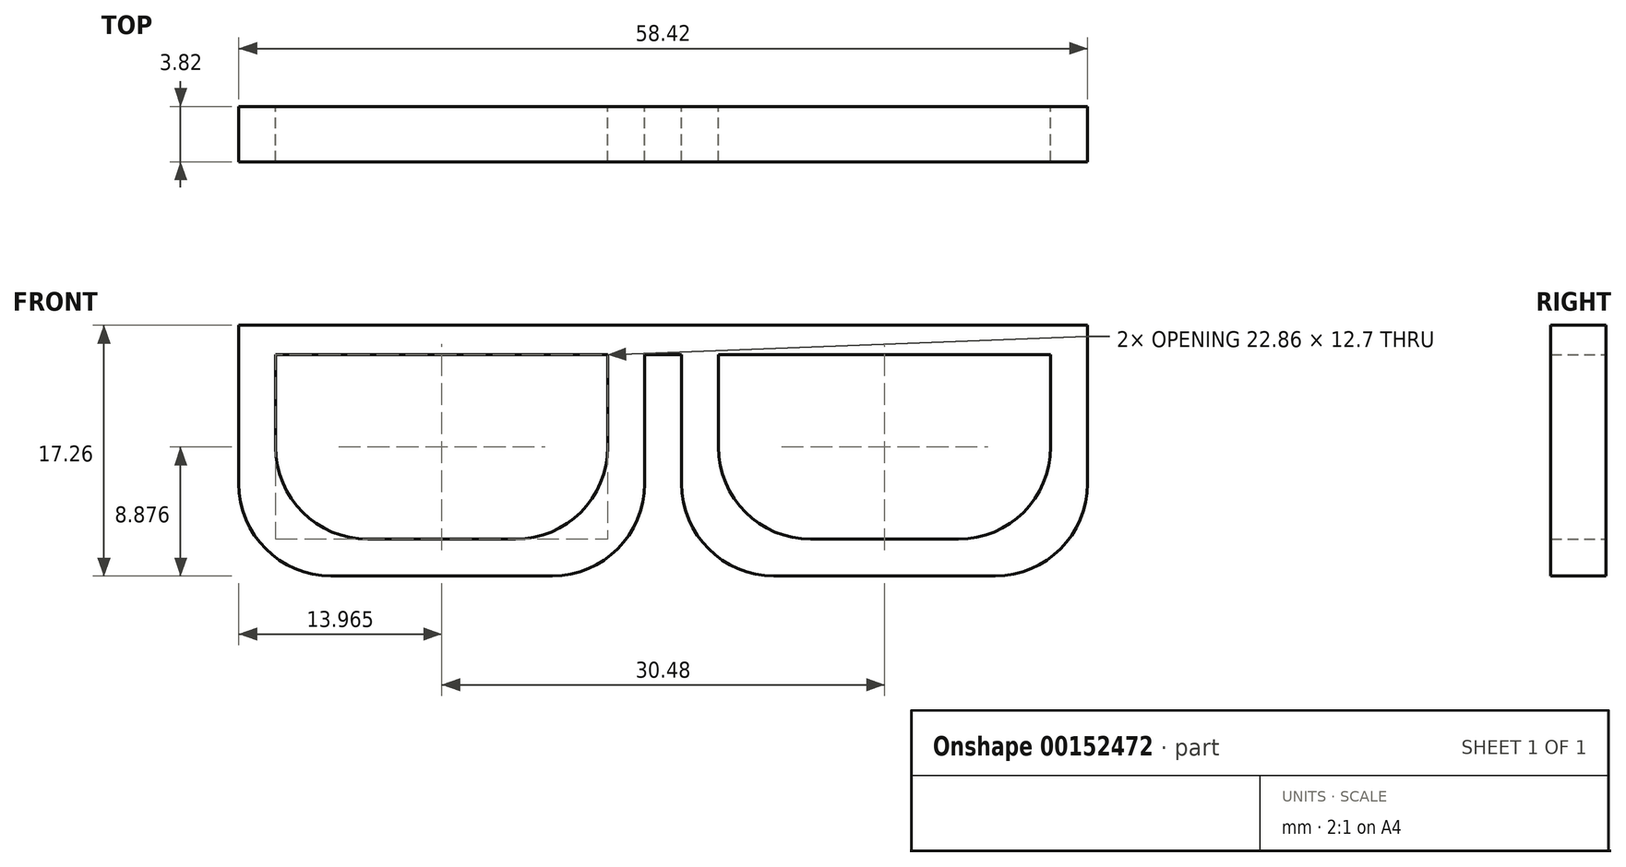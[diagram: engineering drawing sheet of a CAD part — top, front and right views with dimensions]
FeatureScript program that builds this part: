
annotation { "Feature Type Name" : "Feature", "Feature Type Description" : "" }
export const myFeature = defineFeature(function(context is Context, id is Id, definition is map)
    precondition{}
    {
        {
            var Q0;
            Q0=qCreatedBy(makeId("Front.planeOp"),FACE);
            var sketch = newSketch(context, id + "F0", { "sketchPlane" : qUnion([Q0])});
            skLineSegment(sketch, "E0", {"start": v(-55.8, 24.47) * mm, "end": v(-32.94, 24.47) * mm});
            skLineSegment(sketch, "E1", {"start": v(-32.94, 24.47) * mm, "end": v(-32.94, 18.12) * mm});
            skLineSegment(sketch, "E2", {"start": v(-39.3, 11.77) * mm, "end": v(-49.45, 11.77) * mm});
            skLineSegment(sketch, "E3", {"start": v(-55.8, 18.12) * mm, "end": v(-55.8, 24.47) * mm});
            skLineSegment(sketch, "E4", {"start": v(-55.8, 24.47) * mm, "end": v(-2.46, 24.47) * mm});
            skLineSegment(sketch, "E5", {"start": v(-2.46, 24.47) * mm, "end": v(-2.46, 18.12) * mm});
            skLineSegment(sketch, "E6", {"start": v(-8.81, 11.77) * mm, "end": v(-18.97, 11.77) * mm});
            skLineSegment(sketch, "E7", {"start": v(-25.32, 18.12) * mm, "end": v(-25.32, 24.47) * mm});
            skLineSegment(sketch, "E8", {"start": v(-32.94, 22.23) * mm, "end": v(-25.32, 22.23) * mm});
            skPoint(sketch, "E9.visualSharp", {"position": v(-2.46, 11.77) * mm});
            skArc(sketch, "E9.filletArc", {"start": v(-8.81, 11.77) * mm, "mid": v(-4.32, 13.63) * mm, "end": v(-2.46, 18.12) * mm});
            skPoint(sketch, "E10.visualSharp", {"position": v(-25.32, 11.77) * mm});
            skArc(sketch, "E10.filletArc", {"start": v(-25.32, 18.12) * mm, "mid": v(-23.46, 13.63) * mm, "end": v(-18.97, 11.77) * mm});
            skPoint(sketch, "E11.visualSharp", {"position": v(-55.8, 11.77) * mm});
            skArc(sketch, "E11.filletArc", {"start": v(-55.8, 18.12) * mm, "mid": v(-53.94, 13.63) * mm, "end": v(-49.45, 11.77) * mm});
            skPoint(sketch, "E12.visualSharp", {"position": v(-32.94, 11.77) * mm});
            skArc(sketch, "E12.filletArc", {"start": v(-39.3, 11.77) * mm, "mid": v(-34.8, 13.63) * mm, "end": v(-32.94, 18.12) * mm});
            skLineSegment(sketch, "E13", {"start": v(-2.46, 24.47) * mm, "end": v(0.08, 24.47) * mm});
            skLineSegment(sketch, "E14", {"start": v(-55.8, 24.47) * mm, "end": v(-58.34, 24.47) * mm});
            skLineSegment(sketch, "E15", {"start": v(-58.34, 24.47) * mm, "end": v(-58.34, 15.59) * mm});
            skLineSegment(sketch, "E16", {"start": v(-30.4, 24.47) * mm, "end": v(-30.4, 15.59) * mm});
            skLineSegment(sketch, "E17", {"start": v(-36.75, 9.24) * mm, "end": v(-52, 9.24) * mm});
            skLineSegment(sketch, "E18", {"start": v(0.08, 24.47) * mm, "end": v(0.08, 15.59) * mm});
            skLineSegment(sketch, "E19", {"start": v(-27.86, 24.47) * mm, "end": v(-27.86, 15.59) * mm});
            skLineSegment(sketch, "E20", {"start": v(-21.51, 9.24) * mm, "end": v(-6.27, 9.24) * mm});
            skPoint(sketch, "E21.visualSharp", {"position": v(-27.86, 9.24) * mm});
            skArc(sketch, "E21.filletArc", {"start": v(-27.86, 15.59) * mm, "mid": v(-26, 11.1) * mm, "end": v(-21.51, 9.24) * mm});
            skPoint(sketch, "E22.visualSharp", {"position": v(0.08, 9.24) * mm});
            skArc(sketch, "E22.filletArc", {"start": v(-6.27, 9.24) * mm, "mid": v(-1.78, 11.1) * mm, "end": v(0.08, 15.59) * mm});
            skPoint(sketch, "E23.visualSharp", {"position": v(-30.4, 9.24) * mm});
            skArc(sketch, "E23.filletArc", {"start": v(-36.75, 9.24) * mm, "mid": v(-32.26, 11.1) * mm, "end": v(-30.4, 15.59) * mm});
            skPoint(sketch, "E24.visualSharp", {"position": v(-58.34, 9.24) * mm});
            skArc(sketch, "E24.filletArc", {"start": v(-58.34, 15.59) * mm, "mid": v(-56.48, 11.1) * mm, "end": v(-52, 9.24) * mm});
            skLineSegment(sketch, "E25", {"start": v(-58.34, 24.47) * mm, "end": v(-58.34, 26.5) * mm});
            skLineSegment(sketch, "E26", {"start": v(-58.34, 26.5) * mm, "end": v(0.08, 26.5) * mm});
            skLineSegment(sketch, "E27", {"start": v(0.08, 26.5) * mm, "end": v(0.08, 24.47) * mm});
            skSolve(sketch);
        }
        {
            var Q0;
            {var subQ6=sQuery(id+"F0.wireOp",EDGE,"E13");Q0=makeQuery(id+"F0.imprint","IMPRINT",FACE,{"disambiguationData":[TD([[makeQuery(id+"F0.imprint","IMPRINT",EDGE,{"derivedFrom":subQ6}),1.0]])]});}
            var Q1;
            Q1=makeQuery(id+"F0.imprint","IMPRINT",FACE,{"disambiguationData":[TD([[makeQuery(id+"F0.imprint","IMPRINT",EDGE,{"derivedFrom":sQuery(id+"F0.wireOp",EDGE,"E2")}),1.0]])]});
            var Q2;
            Q2=makeQuery(id+"F0.imprint","IMPRINT",FACE,{"disambiguationData":[TD([[makeQuery(id+"F0.imprint","IMPRINT",EDGE,{"derivedFrom":sQuery(id+"F0.wireOp",EDGE,"E5")}),1.0]])]});
            var Q3;
            {var subQ0=sQuery(id+"F0.wireOp",EDGE,"E7");var subQ1=sQuery(id+"F0.wireOp",EDGE,"E4");var subQ2=makeQuery(id+"F0.imprint","INTERSECT",VERTEX,{"derivedFrom":[subQ1,subQ0]});Q3=makeQuery(id+"F0.imprint","IMPRINT",FACE,{"disambiguationData":[TD([[makeQuery(id+"F0.imprint","IMPRINT",EDGE,{"disambiguationData":[TD([[subQ2,1.0]])],"derivedFrom":subQ1}),-1.0]])]});}
            var Q4;
            {var subQ0=sQuery(id+"F0.wireOp",EDGE,"E4");var subQ1=sQuery(id+"F0.wireOp",EDGE,"E1");var subQ2=makeQuery(id+"F0.imprint","INTERSECT",VERTEX,{"derivedFrom":[subQ1,subQ0]});Q4=makeQuery(id+"F0.imprint","IMPRINT",FACE,{"disambiguationData":[TD([[makeQuery(id+"F0.imprint","IMPRINT",EDGE,{"disambiguationData":[TD([[subQ2,-1.0]])],"derivedFrom":subQ1}),1.0]])]});}
            extrude(context, id + "F1", {"entities" : qUnion([Q0, Q1, Q2, Q3, Q4]), "endBound" : BoundingType.SYMMETRIC, "depth" : 3.8 * mm});
        }
    });
